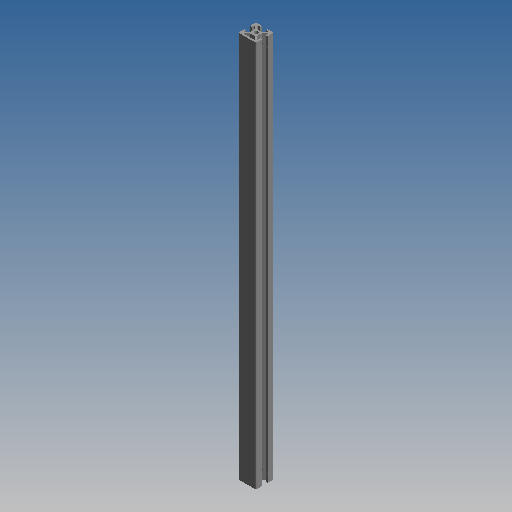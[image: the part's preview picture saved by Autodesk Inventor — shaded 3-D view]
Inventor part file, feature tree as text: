
AUTODESK INVENTOR PART (.ipt)
format: ipt  version: 2020 (Build 240168000, 168)  size: 296,960 bytes
history: native  units: mm (DEFAULTED — no unit token found)
features: other x7, sketch x4, revolve x2, extrude x1, hole x1
ambient origin geometry x8: Origin, YZ Plane, XZ Plane, XY Plane, X Axis, Y Axis, Z Axis, Center Point
bodies: Solid1 (feature_tree)
feature tree (15):
  extrude  "Extrusion1"  TaperAngle=360.0deg  [1 undecoded]
  hole  "Hole1"  [1 undecoded]
  revolve  "Revolution1"  [1 undecoded]
  revolve  "Revolution2"  [1 undecoded]
  other  "C1_XY"
  other  "C1_YZ"
  other  "C1_ZX"
  other  "C1_X"
  other  "C1_Y"
  other  "C1_Z"
  other  "C1_Center"
  sketch  "Sketch_76"
  sketch  "Sketch2"  dims[d0=437.0mm d1=0.0mm]
  sketch  "Sketch_50"  dims[d2=4.2mm d3=6.0mm d4=4.0mm d5=2.0mm d6=90.0deg d7=437.0mm d8=0.0mm d9=360.0deg]
  sketch  "Sketch_51"  dims[d10=360.0deg d11=0.0mm]
note: 4 required parameter values undecoded (feature->parameter linkage not recoverable at this tier; creation-order binding heuristic only, values carry confidence <= 0.55)
